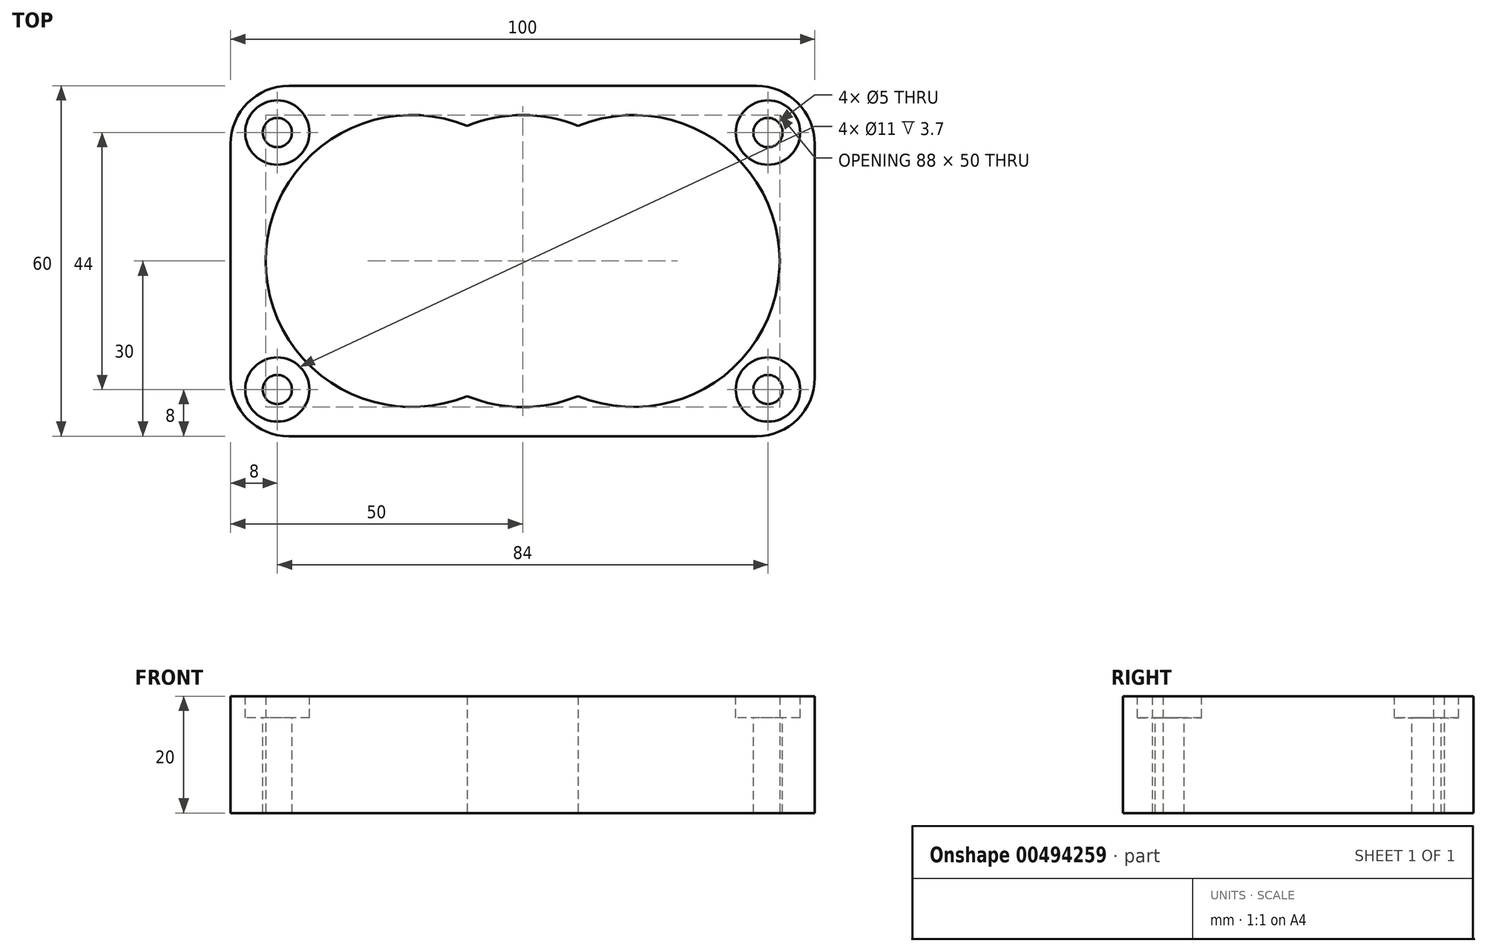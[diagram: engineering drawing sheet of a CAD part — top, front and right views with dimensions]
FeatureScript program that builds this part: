
annotation { "Feature Type Name" : "Feature", "Feature Type Description" : "" }
export const myFeature = defineFeature(function(context is Context, id is Id, definition is map)
    precondition{}
    {
        {
            var Q0;
            Q0=qCreatedBy(makeId("Top.planeOp"),FACE);
            var sketch = newSketch(context, id + "F0", { "sketchPlane" : qUnion([Q0])});
            skLineSegment(sketch, "E0.bottom", {"start": v(40, 30) * mm, "end": v(-40, 30) * mm});
            skLineSegment(sketch, "E0.top", {"start": v(40, -30) * mm, "end": v(-40, -30) * mm});
            skLineSegment(sketch, "E0.left", {"start": v(50, 20) * mm, "end": v(50, -20) * mm});
            skLineSegment(sketch, "E0.right", {"start": v(-50, 20) * mm, "end": v(-50, -20) * mm});
            skPoint(sketch, "E0.middle", {"position": v(0, 0) * mm});
            skPoint(sketch, "E1.visualSharp", {"position": v(50, 30) * mm});
            skArc(sketch, "E1.filletArc", {"start": v(50, 20) * mm, "mid": v(47.07, 27.07) * mm, "end": v(40, 30) * mm});
            skPoint(sketch, "E2.visualSharp", {"position": v(-50, 30) * mm});
            skArc(sketch, "E2.filletArc", {"start": v(-40, 30) * mm, "mid": v(-47.07, 27.07) * mm, "end": v(-50, 20) * mm});
            skPoint(sketch, "E3.visualSharp", {"position": v(-50, -30) * mm});
            skArc(sketch, "E3.filletArc", {"start": v(-50, -20) * mm, "mid": v(-47.07, -27.07) * mm, "end": v(-40, -30) * mm});
            skPoint(sketch, "E4.visualSharp", {"position": v(50, -30) * mm});
            skArc(sketch, "E4.filletArc", {"start": v(40, -30) * mm, "mid": v(47.07, -27.07) * mm, "end": v(50, -20) * mm});
            skCircle(sketch, "E5", {"center": v(0, 0) * mm, "radius": 25 * mm});
            skCircle(sketch, "E6", {"center": v(19, 0) * mm, "radius": 25 * mm});
            skLineSegment(sketch, "E7", {"start": v(0, 30) * mm, "end": v(0, -30) * mm, "construction": true});
            skCircle(sketch, "E8.MirrorC", {"center": v(-19, 0) * mm, "radius": 25 * mm});
            skPoint(sketch, "E9", {"position": v(40, 24) * mm});
            skPoint(sketch, "E10.MirrorP", {"position": v(-40, 24) * mm});
            skLineSegment(sketch, "E11", {"start": v(-50, 2.26) * mm, "end": v(50, 2.26) * mm, "construction": true});
            skPoint(sketch, "E12.MirrorP", {"position": v(-40, -19.48) * mm});
            skSolve(sketch);
        }
        {
            var Q0;
            Q0=makeQuery(id+"F0.imprint","IMPRINT",FACE,{"disambiguationData":[TD([[makeQuery(id+"F0.imprint","IMPRINT",EDGE,{"derivedFrom":sQuery(id+"F0.wireOp",EDGE,"E0.bottom")}),1.0]])]});
            extrude(context, id + "F1", {"entities" : qUnion([Q0]), "depth" : 10 * mm, "hasSecondDirection" : true, "secondDirectionOppositeDirection" : true, "secondDirectionDepth" : 10 * mm});
        }
        {
            var Q0;
            Q0=makeQuery(id+"F1.opExtrude","CAP_FACE",FACE,{"disambiguationData":[OSD([sQuery(id+"F0.wireOp",EDGE,"E0.bottom"),sQuery(id+"F0.wireOp",EDGE,"E0.top"),sQuery(id+"F0.wireOp",EDGE,"E0.left"),sQuery(id+"F0.wireOp",EDGE,"E0.right"),sQuery(id+"F0.wireOp",EDGE,"E1.filletArc"),sQuery(id+"F0.wireOp",EDGE,"E2.filletArc"),sQuery(id+"F0.wireOp",EDGE,"E3.filletArc"),sQuery(id+"F0.wireOp",EDGE,"E4.filletArc"),sQuery(id+"F0.wireOp",EDGE,"E5"),sQuery(id+"F0.wireOp",EDGE,"E6"),sQuery(id+"F0.wireOp",EDGE,"E8.MirrorC")])],"isStart":false});
            var sketch = newSketch(context, id + "F2", { "sketchPlane" : qUnion([Q0])});
            skPoint(sketch, "E13", {"position": v(-42, -22) * mm});
            skLineSegment(sketch, "E14", {"start": v(0, -30) * mm, "end": v(0, 30) * mm, "construction": true});
            skLineSegment(sketch, "E15", {"start": v(50, 0) * mm, "end": v(-50, 0) * mm, "construction": true});
            skPoint(sketch, "E16.MirrorP", {"position": v(42, -22) * mm});
            skPoint(sketch, "E17.MirrorP", {"position": v(42, 22) * mm});
            skPoint(sketch, "E18.MirrorP", {"position": v(-42, 22) * mm});
            skSolve(sketch);
        }
        {
            var Q0;
            Q0=sQuery(id+"F2.wireOp",VERTEX,"E13");
            var Q1;
            Q1=sQuery(id+"F2.wireOp",VERTEX,"E18.MirrorP");
            var Q2;
            Q2=sQuery(id+"F2.wireOp",VERTEX,"E17.MirrorP");
            var Q3;
            Q3=sQuery(id+"F2.wireOp",VERTEX,"E16.MirrorP");
            var Q4;
            Q4=makeQuery(id+"F1.opExtrude","SWEPT_BODY",BODY,{"disambiguationData":[OSD([sQuery(id+"F0.wireOp",EDGE,"E0.bottom"),sQuery(id+"F0.wireOp",EDGE,"E0.top"),sQuery(id+"F0.wireOp",EDGE,"E0.left"),sQuery(id+"F0.wireOp",EDGE,"E0.right"),sQuery(id+"F0.wireOp",EDGE,"E1.filletArc"),sQuery(id+"F0.wireOp",EDGE,"E2.filletArc"),sQuery(id+"F0.wireOp",EDGE,"E3.filletArc"),sQuery(id+"F0.wireOp",EDGE,"E4.filletArc"),sQuery(id+"F0.wireOp",EDGE,"E5"),sQuery(id+"F0.wireOp",EDGE,"E6"),sQuery(id+"F0.wireOp",EDGE,"E8.MirrorC")])]});
            hole(context, id + "F3", {"style" : HoleStyle.C_BORE, "endStyle" : HoleEndStyle.THROUGH, "holeDiameter" : 5 * mm, "cBoreDiameter" : 11 * mm, "cBoreDepth" : 3.7 * mm, "isTappedThrough" : true, "tappedDepth" : 12 * mm, "tapClearance" : 3, "startFromSketch" : true, "locations" : qUnion([Q0, Q1, Q2, Q3]), "scope" : qUnion([Q4])});
        }
    });
